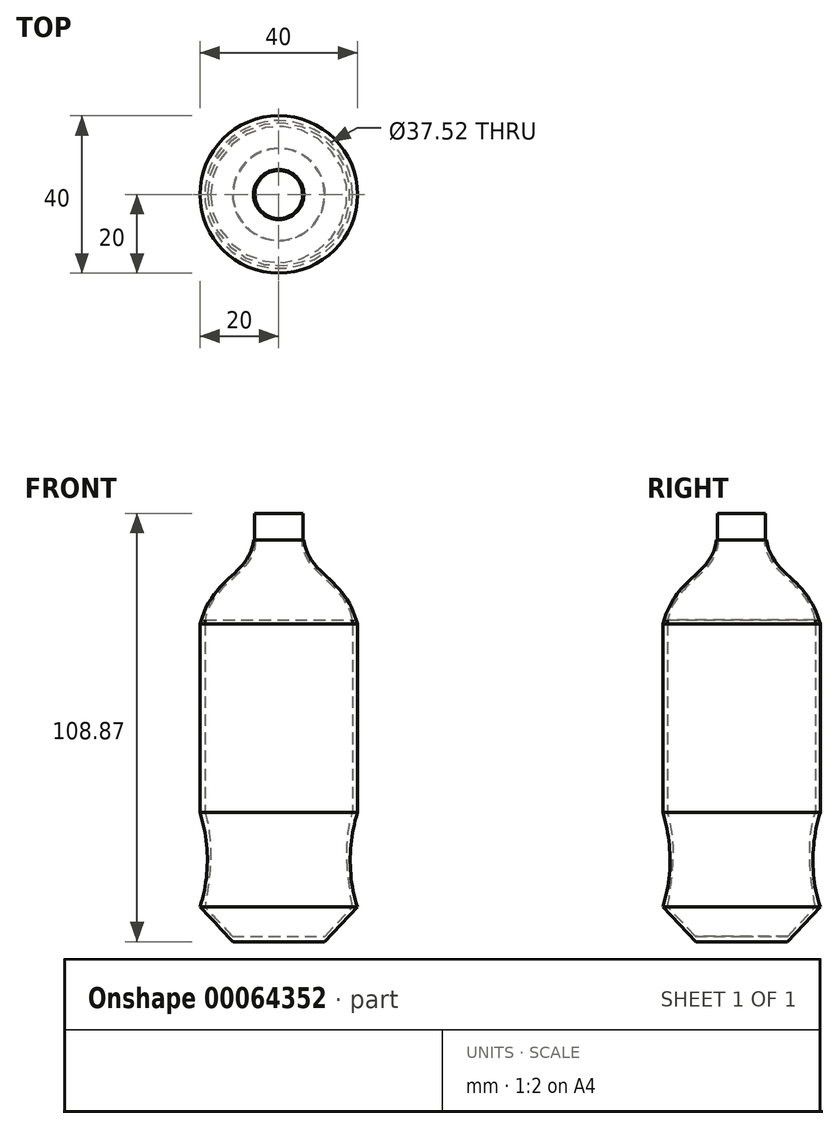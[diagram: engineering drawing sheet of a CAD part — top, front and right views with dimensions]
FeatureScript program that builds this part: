
annotation { "Feature Type Name" : "Feature", "Feature Type Description" : "" }
export const myFeature = defineFeature(function(context is Context, id is Id, definition is map)
    precondition{}
    {
        {
            var Q0;
            Q0=qCreatedBy(makeId("Right.planeOp"),FACE);
            var sketch = newSketch(context, id + "F0", { "sketchPlane" : qUnion([Q0])});
            skLineSegment(sketch, "E0", {"start": v(0, -32.92) * mm, "end": v(11.62, -32.92) * mm});
            skLineSegment(sketch, "E1", {"start": v(11.62, -32.92) * mm, "end": v(20, -24.06) * mm});
            skFitSpline(sketch, "E2", {"points": [v(20, -24.06) * mm, v(20, 0) * mm], "startDerivative": vector(-7.8, 23.83) * mm, "endDerivative": vector(7.03, 23.17) * mm});
            skLineSegment(sketch, "E3", {"start": v(20, 0) * mm, "end": v(20, 47.86) * mm});
            skFitSpline(sketch, "E4", {"points": [v(20, 47.86) * mm, v(6.37, 69.11) * mm], "startDerivative": vector(-10.2, 36.93) * mm, "endDerivative": vector(-3.74, 27.43) * mm});
            skLineSegment(sketch, "E5", {"start": v(0, -53.97) * mm, "end": v(0, 75.95) * mm});
            skLineSegment(sketch, "E6", {"start": v(6.37, 69.11) * mm, "end": v(0, 69.11) * mm});
            skFitSpline(sketch, "E7", {"points": [v(5.86, 69.11) * mm, v(18.76, 48.86) * mm], "startDerivative": vector(1.7, -27.43) * mm, "endDerivative": vector(6.49, -30.18) * mm});
            skLineSegment(sketch, "E8", {"start": v(18.76, 48.86) * mm, "end": v(18.76, 0) * mm});
            skFitSpline(sketch, "E9", {"points": [v(18.76, 0) * mm, v(18.76, -24.07) * mm], "startDerivative": vector(-7.22, -23.17) * mm, "endDerivative": vector(4.1, -23.88) * mm});
            skLineSegment(sketch, "E10", {"start": v(18.76, -24.07) * mm, "end": v(11.76, -31.49) * mm});
            skLineSegment(sketch, "E11", {"start": v(11.76, -31.49) * mm, "end": v(0, -31.49) * mm});
            skLineSegment(sketch, "E12", {"start": v(5.86, 69.11) * mm, "end": v(6.36, 69.11) * mm});
            skLineSegment(sketch, "E13", {"start": v(6.11, 69.11) * mm, "end": v(6.11, 75.95) * mm});
            skPoint(sketch, "E13.endSnap0", {"position": v(6.11, 69.11) * mm});
            skLineSegment(sketch, "E14", {"start": v(6.11, 75.95) * mm, "end": v(0, 75.95) * mm});
            skLineSegment(sketch, "E15", {"start": v(0, 75.95) * mm, "end": v(0, 76.46) * mm});
            skSolve(sketch);
        }
        {
            var Q0;
            {var subQ1=sQuery(id+"F0.wireOp",EDGE,"E0");Q0=makeQuery(id+"F0.imprint","IMPRINT",FACE,{"disambiguationData":[TD([[makeQuery(id+"F0.imprint","IMPRINT",EDGE,{"derivedFrom":subQ1}),1.0]])]});}
            var Q1;
            {var subQ0=sQuery(id+"F0.wireOp",EDGE,"E13");Q1=makeQuery(id+"F0.imprint","IMPRINT",FACE,{"disambiguationData":[TD([[makeQuery(id+"F0.imprint","IMPRINT",EDGE,{"derivedFrom":subQ0}),1.0]])]});}
            var Q2;
            Q2=sQuery(id+"F0.wireOp",EDGE,"E5");
            revolve(context, id + "F1", {"entities" : qUnion([Q0, Q1]), "axis" : qUnion([Q2]), "revolveType" : RevolveType.FULL});
        }
    });
